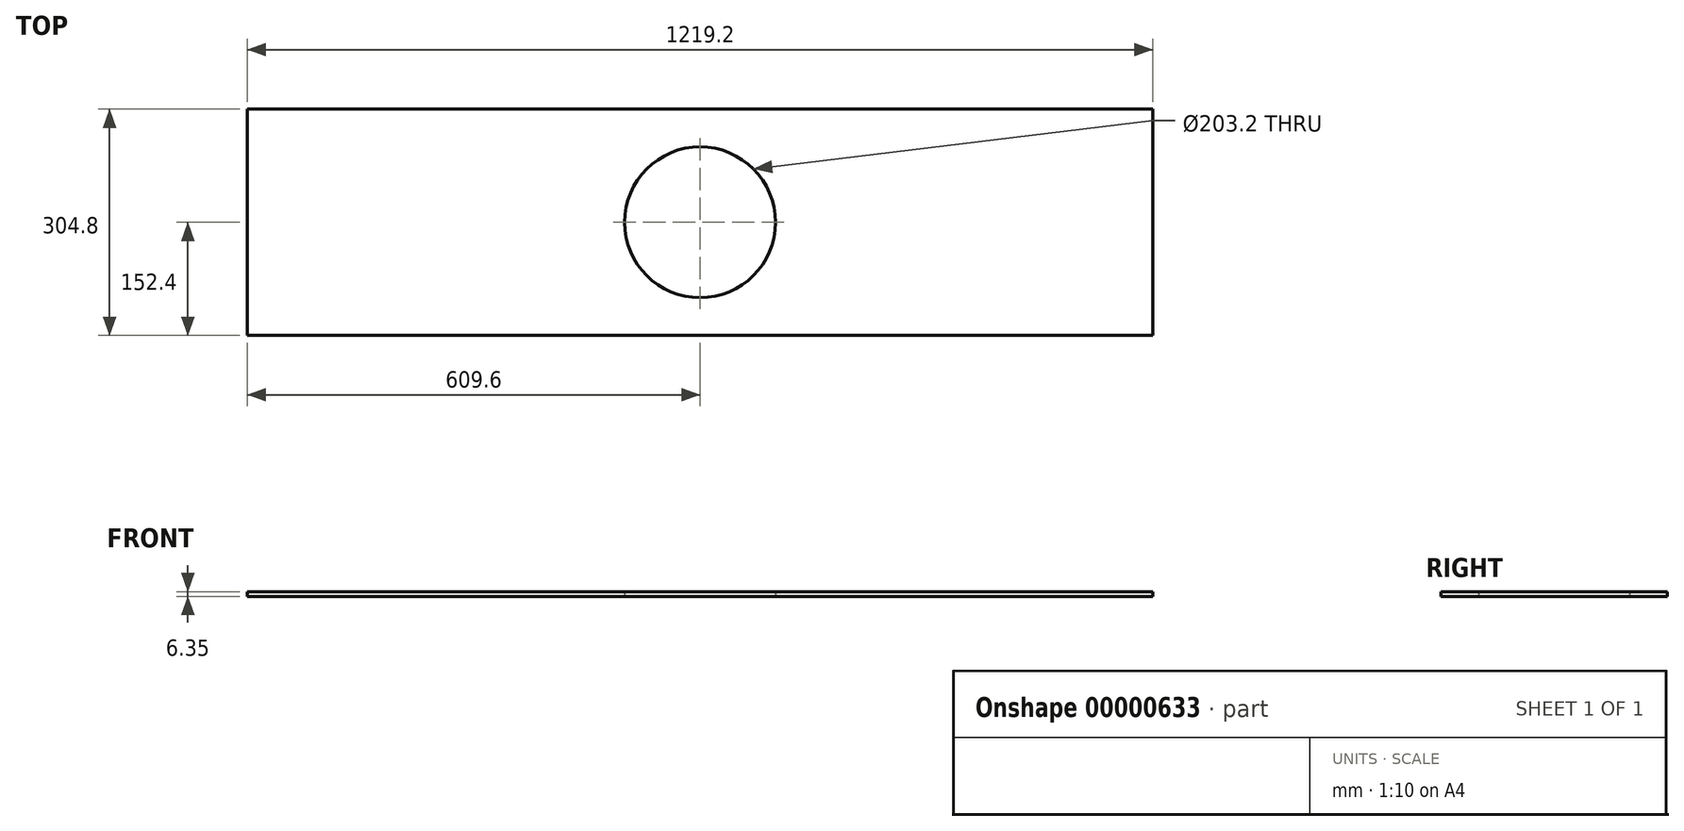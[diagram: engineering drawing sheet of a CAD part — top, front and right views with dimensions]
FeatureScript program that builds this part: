
annotation { "Feature Type Name" : "Feature", "Feature Type Description" : "" }
export const myFeature = defineFeature(function(context is Context, id is Id, definition is map)
    precondition{}
    {
        {
            var Q0;
            Q0=qCreatedBy(makeId("Top.planeOp"),FACE);
            var sketch = newSketch(context, id + "F0", { "sketchPlane" : qUnion([Q0])});
            skLineSegment(sketch, "E0", {"start": v(0, 0) * mm, "end": v(1219.2, 0) * mm});
            skLineSegment(sketch, "E1", {"start": v(1219.2, 0) * mm, "end": v(1219.2, 304.8) * mm});
            skLineSegment(sketch, "E2", {"start": v(1219.2, 304.8) * mm, "end": v(0, 304.8) * mm});
            skLineSegment(sketch, "E3", {"start": v(0, 304.8) * mm, "end": v(0, 0) * mm});
            skCircle(sketch, "E4", {"center": v(609.6, 152.4) * mm, "radius": 101.6 * mm});
            skLineSegment(sketch, "E5", {"start": v(0, 152.4) * mm, "end": v(1219.2, 152.4) * mm, "construction": true});
            skSolve(sketch);
        }
        {
            var Q0;
            Q0=makeQuery(id+"F0.imprint","IMPRINT",FACE,{"disambiguationData":[TD([[makeQuery(id+"F0.imprint","IMPRINT",EDGE,{"derivedFrom":sQuery(id+"F0.wireOp",EDGE,"E0")}),1.0]])]});
            extrude(context, id + "F1", {"entities" : qUnion([Q0]), "depth" : 6.35 * mm});
        }
    });
